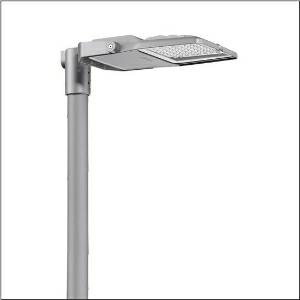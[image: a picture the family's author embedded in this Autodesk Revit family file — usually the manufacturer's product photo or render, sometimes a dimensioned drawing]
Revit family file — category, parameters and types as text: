
# Revit family: floodlight_fl_21_mini___pl33t_5xa7776c2f3a_ca81
name_source: partatom
category: Lighting Fixtures
units: mm (PartAtom-declared; Revit-internal decimal feet)

## family parameters
Cut with Voids When Loaded = No
Host = Face
Light Source = No
Part Type = Normal
Room Calculation Point = No
Round Connector Dimension = Use Diameter
Shared = No

## types (1)
- --- (1 x LED, 12050 lm, 89 W, 3000K)
    Apparent Load = 89 VA
    CIE Flux Codes = 26 75 99 100 100
    Color Rendering = 70
    Color Temperature = 3000K
    Default Elevation = 1800 mm
    Description = Floodlight FL 21 mini, floodlight, primary light control with lens, of PMMA, primary optical cover: protective disc, of toughened safety glass, transparent, light distribution: PL33T, light emission: direct distribution, installation type: surface-mounted, LED, High Power LED, rated luminous flux: 12.050lm, luminous efficacy: 135lm/W, light colour: 730, colour temperature: 3000K, control gear: Smart Interface (Zhaga), control: flexible luminous flux parameterisation, time-dependent luminous flux control, constant luminous flux control, overheat protection, pre-setting: logarithmic dimming characteristic, with terminal, 6-pole, mains connection: 220..240V, AC, 50/60Hz, start of lifetime: 89W, end of service life: 94W, reduction: 43W, luminaire housing, of diecast aluminium, powder-coated, Siteco® metallic grey (DB 702S), corrosivity category C5 mid according to DIN EN ISO 12944, suitable for swimming pools, chlorine-resistant, sealing non-destructively replaceable, please order mast flange separately, mast bracket, of steel, galvanised, powder-coated, Siteco® metallic grey (DB 702S), Smart Interface below and above, protection rating (complete): IP66, insulation class (complete): insulation class II (safety insulation), certification: CE, ENEC, VDE, protection symbol: D, impact resistance: IK08, permissible operating ambient temperature: -40..+40°C, permissible operating ambient temperature for outdoor applications: -40..+50°C, standard: DIN EN 12944, LABS conformity tested according to VDMA 24364:2018-05, packaging unit: 1 piece

Light Distribution: PL33T
    Height = 70 mm
    Lamp = 1 x LED
    Lamp Light Flux = 12050 lm
    Lamp Power = 89 W
    Lamp count = 1
    Length = 485 mm
    Luminous efficacy = 135 lm/W
    Manufacturer = Siteco
    ModVariant = No
    Model = 5XA7776C2F3A
    Number of Poles = 1
    OnlyDefault = Yes
    Power Factor = 1
    Product Name = Floodlight FL 21 mini | PL33T
    Product group = floodlight | pylon annexe
    ProductGroupID = 6200
    Protection Class = Protection class II
    Protection Degree = IP 66
    RLX_Detail_Level = 1
    RLX_Emergency_Light_Flux = 0 lm
    RLX_Emergency_Type = 0
    RLX_Emergency_Type_DB = No
    RlxData = <blob elided: 100841 chars, md5=5fe80dd6>
    Socket = socket
    Standby Power = 0 W
    System Light Flux = 12050 lm
    System Power = 89 W
    Type Comments = factory setting: luminous flux: 100 % | dim-lin: 254 | 456 mA
    Type Image = l_1007125.jpg
    URL = http://relux.com
    VarID = @adj_148478
    Voltage = 0 V
    Weight = 0.00 kg
    Width = 337 mm

## geometry (parser evidence)
native form markers: Blend x4, Sweep x13
no freeform markers — native parametric forms only
